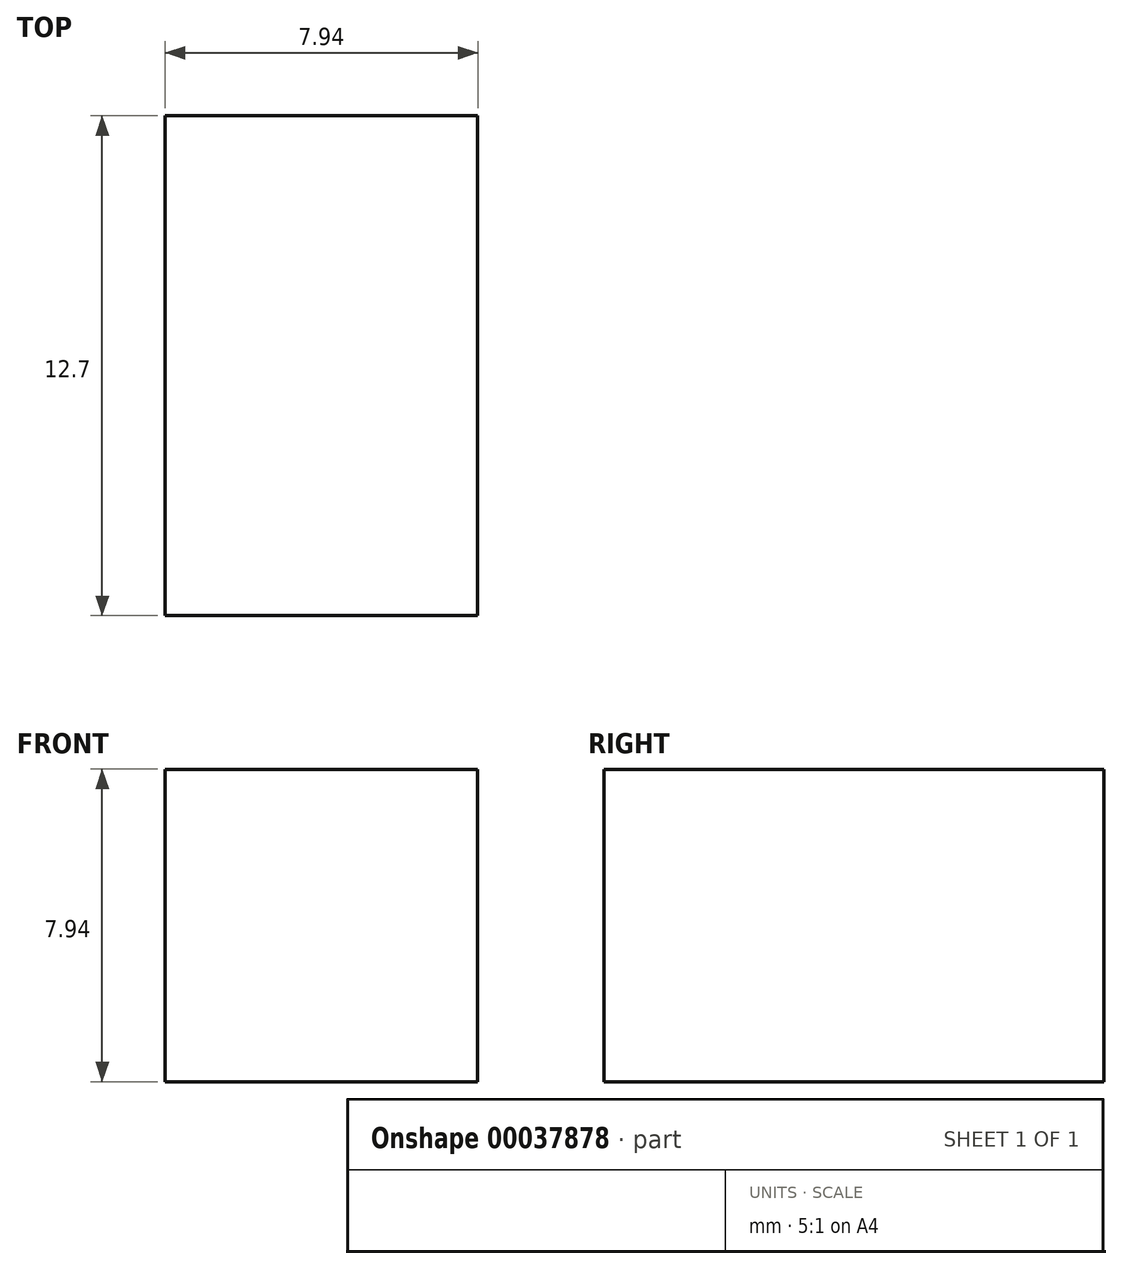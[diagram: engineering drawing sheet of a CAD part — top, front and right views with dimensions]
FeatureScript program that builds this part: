
annotation { "Feature Type Name" : "Feature", "Feature Type Description" : "" }
export const myFeature = defineFeature(function(context is Context, id is Id, definition is map)
    precondition{}
    {
        {
            var Q0;
            Q0=qCreatedBy(makeId("Top.planeOp"),FACE);
            var sketch = newSketch(context, id + "F0", { "sketchPlane" : qUnion([Q0])});
            skLineSegment(sketch, "E0.bottom", {"start": v(0, 0) * mm, "end": v(7.94, 0) * mm});
            skLineSegment(sketch, "E0.top", {"start": v(0, -12.7) * mm, "end": v(7.94, -12.7) * mm});
            skLineSegment(sketch, "E0.left", {"start": v(0, 0) * mm, "end": v(0, -12.7) * mm});
            skLineSegment(sketch, "E0.right", {"start": v(7.94, 0) * mm, "end": v(7.94, -12.7) * mm});
            skSolve(sketch);
        }
        {
            var Q0;
            Q0 = qSketchRegion(id + "F0", true);
            extrude(context, id + "F1", {"entities" : qUnion([Q0]), "depth" : 7.94 * mm});
        }
    });
